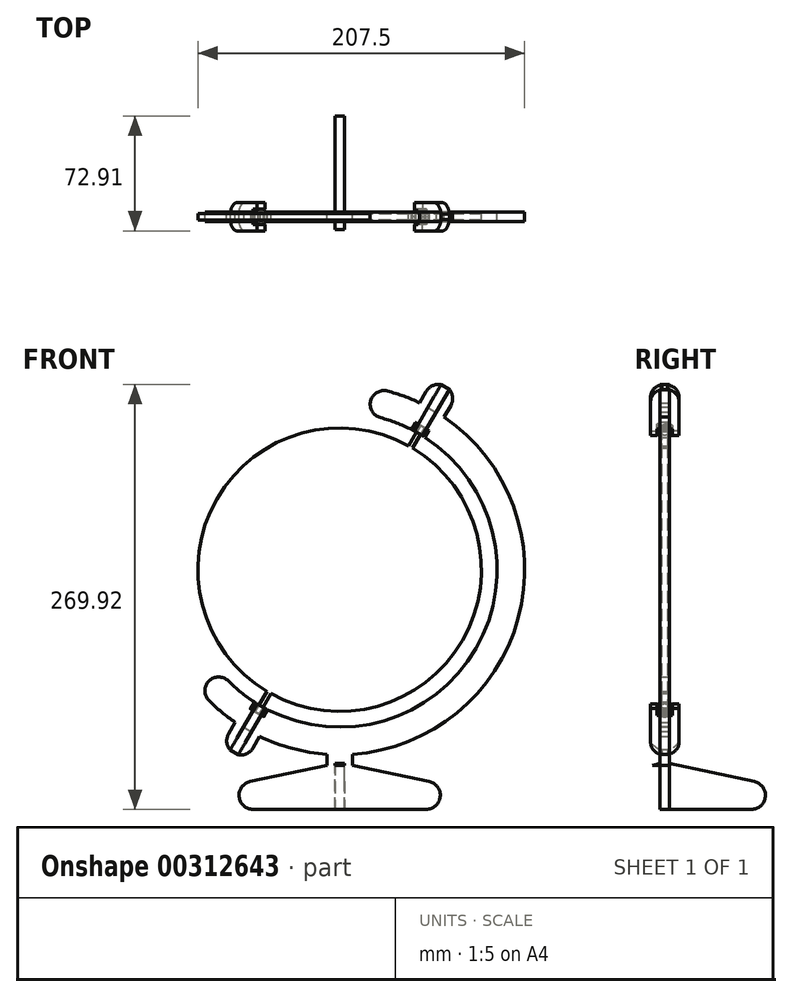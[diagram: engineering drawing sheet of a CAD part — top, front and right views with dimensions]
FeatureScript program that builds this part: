
annotation { "Feature Type Name" : "Feature", "Feature Type Description" : "" }
export const myFeature = defineFeature(function(context is Context, id is Id, definition is map)
    precondition{}
    {
        {
            var Q0;
            Q0=qCreatedBy(makeId("Front.planeOp"),FACE);
            var sketch = newSketch(context, id + "F0", { "sketchPlane" : qUnion([Q0])});
            skLineSegment(sketch, "E0", {"start": v(-16.98, 17.96) * mm, "end": v(-16.98, 0) * mm, "construction": true});
            skLineSegment(sketch, "E1", {"start": v(-16.98, 0) * mm, "end": v(0, 0) * mm, "construction": true});
            skLineSegment(sketch, "E2", {"start": v(-16.98, 17.96) * mm, "end": v(-16.98, 117.96) * mm, "construction": true});
            skLineSegment(sketch, "E3", {"start": v(-16.98, 17.96) * mm, "end": v(8.9, 114.55) * mm, "construction": true});
            skLineSegment(sketch, "E4", {"start": v(8.9, 114.55) * mm, "end": v(13.43, 131.46) * mm, "construction": true});
            skLineSegment(sketch, "E5", {"start": v(-16.98, 17.96) * mm, "end": v(-87.7, -52.75) * mm, "construction": true});
            skLineSegment(sketch, "E6", {"start": v(-87.7, -52.75) * mm, "end": v(-100.07, -65.12) * mm, "construction": true});
            skArc(sketch, "E7", {"start": v(8.9, 114.55) * mm, "mid": v(-103.58, 67.96) * mm, "end": v(-87.7, -52.75) * mm, "construction": true});
            skArc(sketch, "E8", {"start": v(-87.7, -52.75) * mm, "mid": v(69.62, -32.04) * mm, "end": v(8.9, 114.55) * mm});
            skArc(sketch, "E9", {"start": v(-100.07, -65.12) * mm, "mid": v(-92.03, -72.45) * mm, "end": v(-83.35, -79) * mm});
            skArc(sketch, "E10", {"start": v(8.9, 114.55) * mm, "mid": v(2.71, 125.27) * mm, "end": v(13.43, 131.46) * mm});
            skArc(sketch, "E11", {"start": v(-100.07, -65.12) * mm, "mid": v(-100.07, -52.75) * mm, "end": v(-87.7, -52.75) * mm});
            skLineSegment(sketch, "E12", {"start": v(-16.98, 17.96) * mm, "end": v(33.02, 104.56) * mm, "construction": true});
            skLineSegment(sketch, "E13", {"start": v(-16.98, 17.96) * mm, "end": v(-66.98, -68.64) * mm, "construction": true});
            skLineSegment(sketch, "E14", {"start": v(-66.98, -68.64) * mm, "end": v(-75.73, -83.8) * mm, "construction": true});
            skLineSegment(sketch, "E15", {"start": v(33.02, 104.56) * mm, "end": v(41.77, 119.72) * mm, "construction": true});
            skLineSegment(sketch, "E16", {"start": v(33.8, 123.92) * mm, "end": v(37.97, 131.15) * mm});
            skLineSegment(sketch, "E17", {"start": v(49.39, 114.92) * mm, "end": v(53.56, 122.15) * mm});
            skLineSegment(sketch, "E18", {"start": v(41.77, 119.72) * mm, "end": v(45.77, 126.65) * mm, "construction": true});
            skLineSegment(sketch, "E19", {"start": v(45.77, 126.65) * mm, "end": v(53.56, 122.15) * mm, "construction": true});
            skLineSegment(sketch, "E20", {"start": v(45.77, 126.65) * mm, "end": v(37.97, 131.15) * mm, "construction": true});
            skArc(sketch, "E21", {"start": v(37.97, 131.15) * mm, "mid": v(50.27, 134.44) * mm, "end": v(53.56, 122.15) * mm});
            skLineSegment(sketch, "E22", {"start": v(-75.73, -83.8) * mm, "end": v(-79.73, -90.72) * mm, "construction": true});
            skLineSegment(sketch, "E23", {"start": v(-67.77, -88) * mm, "end": v(-71.94, -95.22) * mm});
            skLineSegment(sketch, "E24", {"start": v(-71.94, -95.22) * mm, "end": v(-79.73, -90.72) * mm, "construction": true});
            skLineSegment(sketch, "E25", {"start": v(-79.73, -90.72) * mm, "end": v(-87.53, -86.22) * mm, "construction": true});
            skLineSegment(sketch, "E26", {"start": v(-87.53, -86.22) * mm, "end": v(-83.35, -79) * mm});
            skArc(sketch, "E27", {"start": v(-87.53, -86.22) * mm, "mid": v(-84.23, -98.52) * mm, "end": v(-71.94, -95.22) * mm});
            skArc(sketch, "E28", {"start": v(-83.35, -79) * mm, "mid": v(-75.73, -83.8) * mm, "end": v(-67.77, -88) * mm, "construction": true});
            skArc(sketch, "E29", {"start": v(-67.77, -88) * mm, "mid": v(-46.9, -95.66) * mm, "end": v(-24.98, -99.27) * mm});
            skArc(sketch, "E30", {"start": v(33.8, 123.92) * mm, "mid": v(23.79, 128.16) * mm, "end": v(13.43, 131.46) * mm});
            skArc(sketch, "E31", {"start": v(49.39, 114.92) * mm, "mid": v(41.77, 119.72) * mm, "end": v(33.8, 123.92) * mm, "construction": true});
            skLineSegment(sketch, "E32", {"start": v(-24.98, -99.27) * mm, "end": v(-24.98, -106.27) * mm});
            skLineSegment(sketch, "E33", {"start": v(-16.98, 17.96) * mm, "end": v(-16.98, -82.04) * mm, "construction": true});
            skLineSegment(sketch, "E34", {"start": v(-16.98, -82.04) * mm, "end": v(-16.98, -99.54) * mm, "construction": true});
            skLineSegment(sketch, "E35", {"start": v(-24.98, -106.27) * mm, "end": v(-16.98, -99.54) * mm, "construction": true});
            skLineSegment(sketch, "E36", {"start": v(-16.98, -134.27) * mm, "end": v(-16.98, -99.54) * mm, "construction": true});
            skLineSegment(sketch, "E37", {"start": v(-24.98, -106.27) * mm, "end": v(-71.98, -116.26) * mm});
            skLineSegment(sketch, "E38", {"start": v(-16.98, -134.27) * mm, "end": v(-71.98, -134.27) * mm});
            skLineSegment(sketch, "E39", {"start": v(-71.98, -134.27) * mm, "end": v(-71.98, -116.26) * mm, "construction": true});
            skLineSegment(sketch, "E40", {"start": v(-71.98, -116.26) * mm, "end": v(-73.83, -116.65) * mm});
            skArc(sketch, "E41", {"start": v(-73.83, -116.65) * mm, "mid": v(-80.84, -126.3) * mm, "end": v(-71.98, -134.27) * mm});
            skArc(sketch, "E42", {"start": v(-71.98, -134.27) * mm, "mid": v(-63.13, -124.43) * mm, "end": v(-73.83, -116.65) * mm, "construction": true});
            skLineSegment(sketch, "E43.MirrorCS", {"start": v(-8.98, -99.27) * mm, "end": v(-8.98, -106.27) * mm});
            skLineSegment(sketch, "E44.MirrorCS", {"start": v(-8.98, -106.27) * mm, "end": v(38.02, -116.26) * mm});
            skLineSegment(sketch, "E45.MirrorCS", {"start": v(38.02, -116.26) * mm, "end": v(39.87, -116.65) * mm});
            skArc(sketch, "E46.MirrorCS", {"start": v(39.87, -116.65) * mm, "mid": v(46.87, -126.3) * mm, "end": v(38.02, -134.27) * mm});
            skLineSegment(sketch, "E47.MirrorCS", {"start": v(-16.98, -134.27) * mm, "end": v(38.02, -134.27) * mm});
            skArc(sketch, "E48", {"start": v(-24.98, -99.27) * mm, "mid": v(-16.98, -99.54) * mm, "end": v(-8.98, -99.27) * mm, "construction": true});
            skArc(sketch, "E49", {"start": v(-8.98, -99.27) * mm, "mid": v(96.38, -12.93) * mm, "end": v(49.39, 114.92) * mm});
            skSolve(sketch);
        }
        {
            var Q0;
            Q0=makeQuery(id+"F0.imprint","IMPRINT",FACE,{"disambiguationData":[TD([[makeQuery(id+"F0.imprint","IMPRINT",EDGE,{"derivedFrom":sQuery(id+"F0.wireOp",EDGE,"E8")}),-1.0]])]});
            extrude(context, id + "F1", {"entities" : qUnion([Q0]), "depth" : 3 * mm, "hasSecondDirection" : true, "secondDirectionOppositeDirection" : true, "secondDirectionDepth" : 3 * mm});
        }
        {
            var Q0;
            Q0=makeQuery(id+"F1.opExtrude","CAP_FACE",FACE,{"disambiguationData":[OSD([sQuery(id+"F0.wireOp",EDGE,"E8"),sQuery(id+"F0.wireOp",EDGE,"E9"),sQuery(id+"F0.wireOp",EDGE,"E10"),sQuery(id+"F0.wireOp",EDGE,"E11"),sQuery(id+"F0.wireOp",EDGE,"E16"),sQuery(id+"F0.wireOp",EDGE,"E17"),sQuery(id+"F0.wireOp",EDGE,"E21"),sQuery(id+"F0.wireOp",EDGE,"E23"),sQuery(id+"F0.wireOp",EDGE,"E26"),sQuery(id+"F0.wireOp",EDGE,"E27"),sQuery(id+"F0.wireOp",EDGE,"E29"),sQuery(id+"F0.wireOp",EDGE,"E30"),sQuery(id+"F0.wireOp",EDGE,"E32"),sQuery(id+"F0.wireOp",EDGE,"E37"),sQuery(id+"F0.wireOp",EDGE,"E38"),sQuery(id+"F0.wireOp",EDGE,"E40"),sQuery(id+"F0.wireOp",EDGE,"E41"),sQuery(id+"F0.wireOp",EDGE,"E43.MirrorCS"),sQuery(id+"F0.wireOp",EDGE,"E44.MirrorCS"),sQuery(id+"F0.wireOp",EDGE,"E45.MirrorCS"),sQuery(id+"F0.wireOp",EDGE,"E46.MirrorCS"),sQuery(id+"F0.wireOp",EDGE,"E47.MirrorCS"),sQuery(id+"F0.wireOp",EDGE,"E49")])],"isStart":false});
            var sketch = newSketch(context, id + "F2", { "sketchPlane" : qUnion([Q0])});
            skLineSegment(sketch, "E50", {"start": v(-24.98, -106.27) * mm, "end": v(-8.98, -106.27) * mm, "construction": true});
            skLineSegment(sketch, "E51", {"start": v(-16.98, -106.27) * mm, "end": v(-16.98, -120.27) * mm, "construction": true});
            skLineSegment(sketch, "E52", {"start": v(-16.98, -120.27) * mm, "end": v(-16.98, -134.27) * mm, "construction": true});
            skLineSegment(sketch, "E53", {"start": v(-16.98, -120.27) * mm, "end": v(-13.98, -120.27) * mm});
            skLineSegment(sketch, "E54", {"start": v(-13.98, -120.27) * mm, "end": v(-13.98, -134.27) * mm});
            skLineSegment(sketch, "E55", {"start": v(-16.98, -120.27) * mm, "end": v(-19.98, -120.27) * mm});
            skLineSegment(sketch, "E56", {"start": v(-19.98, -120.27) * mm, "end": v(-19.98, -134.27) * mm});
            skLineSegment(sketch, "E57", {"start": v(-19.98, -134.27) * mm, "end": v(-16.98, -134.27) * mm});
            skLineSegment(sketch, "E58", {"start": v(-13.98, -134.27) * mm, "end": v(-16.98, -134.27) * mm});
            skSolve(sketch);
        }
        {
            var Q0;
            Q0=makeQuery(id+"F2.imprint","IMPRINT",FACE,{"disambiguationData":[TD([[makeQuery(id+"F2.imprint","IMPRINT",EDGE,{"derivedFrom":sQuery(id+"F2.wireOp",EDGE,"E53")}),-1.0]])]});
            var Q1;
            Q1=makeQuery(id+"F1.opExtrude","CAP_FACE",FACE,{"disambiguationData":[OSD([sQuery(id+"F0.wireOp",EDGE,"E8"),sQuery(id+"F0.wireOp",EDGE,"E9"),sQuery(id+"F0.wireOp",EDGE,"E10"),sQuery(id+"F0.wireOp",EDGE,"E11"),sQuery(id+"F0.wireOp",EDGE,"E16"),sQuery(id+"F0.wireOp",EDGE,"E17"),sQuery(id+"F0.wireOp",EDGE,"E21"),sQuery(id+"F0.wireOp",EDGE,"E23"),sQuery(id+"F0.wireOp",EDGE,"E26"),sQuery(id+"F0.wireOp",EDGE,"E27"),sQuery(id+"F0.wireOp",EDGE,"E29"),sQuery(id+"F0.wireOp",EDGE,"E30"),sQuery(id+"F0.wireOp",EDGE,"E32"),sQuery(id+"F0.wireOp",EDGE,"E37"),sQuery(id+"F0.wireOp",EDGE,"E38"),sQuery(id+"F0.wireOp",EDGE,"E40"),sQuery(id+"F0.wireOp",EDGE,"E41"),sQuery(id+"F0.wireOp",EDGE,"E43.MirrorCS"),sQuery(id+"F0.wireOp",EDGE,"E44.MirrorCS"),sQuery(id+"F0.wireOp",EDGE,"E45.MirrorCS"),sQuery(id+"F0.wireOp",EDGE,"E46.MirrorCS"),sQuery(id+"F0.wireOp",EDGE,"E47.MirrorCS"),sQuery(id+"F0.wireOp",EDGE,"E49")])],"isStart":true});
            extrude(context, id + "F3", {"entities" : qUnion([Q0]), "operationType" : NewBodyOperationType.REMOVE, "endBound" : BoundingType.UP_TO_SURFACE, "oppositeDirection" : true, "endBoundEntityFace" : qUnion([Q1]), "depth" : 25 * mm});
        }
        {
            var Q0;
            Q0=makeQuery(id+"F3.boolean.opBoolean","COPY",FACE,{"derivedFrom":makeQuery(id+"F3.opExtrude","SWEPT_FACE",FACE,{"disambiguationData":[OSD([sQuery(id+"F2.wireOp",EDGE,"E53"),sQuery(id+"F2.wireOp",EDGE,"E55")])]})});
            var Q1;
            {var subQ1=sQuery(id+"F0.wireOp",EDGE,"E47.MirrorCS");var subQ6=sQuery(id+"F0.wireOp",EDGE,"E41");var subQ8=sQuery(id+"F0.wireOp",EDGE,"E38");Q1=makeQuery(id+"F3.boolean.opBoolean","SPLIT",FACE,{"disambiguationData":[TD([makeQuery(id+"F1.opExtrude","SWEPT_FACE",FACE,{"disambiguationData":[OSD([subQ6])]})])],"derivedFrom":makeQuery(id+"F1.opExtrude","SWEPT_FACE",FACE,{"disambiguationData":[OSD([subQ8,subQ1])]})});}
            extrude(context, id + "F4", {"entities" : qUnion([Q0]), "endBound" : BoundingType.UP_TO_SURFACE, "endBoundEntityFace" : qUnion([Q1]), "depth" : 25 * mm});
        }
        {
            var Q0;
            Q0=makeQuery(id+"F4.opExtrude","SWEPT_FACE",FACE,{"disambiguationData":[OSD([sQuery(id+"F2.wireOp",EDGE,"E55"),sQuery(id+"F2.wireOp",EDGE,"E56")])]});
            var sketch = newSketch(context, id + "F5", { "sketchPlane" : qUnion([Q0])});
            skLineSegment(sketch, "E59", {"start": v(0, -134.27) * mm, "end": v(-55, -134.27) * mm});
            skLineSegment(sketch, "E60", {"start": v(0, -134.27) * mm, "end": v(0, -120.27) * mm, "construction": true});
            skLineSegment(sketch, "E61", {"start": v(0, -120.27) * mm, "end": v(0, -106.27) * mm, "construction": true});
            skLineSegment(sketch, "E62", {"start": v(0, -106.27) * mm, "end": v(-8, -106.27) * mm});
            skLineSegment(sketch, "E63", {"start": v(-8, -106.27) * mm, "end": v(-55, -116.26) * mm});
            skLineSegment(sketch, "E64", {"start": v(-55, -116.26) * mm, "end": v(-55, -134.27) * mm, "construction": true});
            skLineSegment(sketch, "E65", {"start": v(-55, -116.26) * mm, "end": v(-56.85, -116.65) * mm});
            skArc(sketch, "E66", {"start": v(-56.85, -116.65) * mm, "mid": v(-63.86, -126.3) * mm, "end": v(-55, -134.27) * mm});
            skArc(sketch, "E67", {"start": v(-55, -134.27) * mm, "mid": v(-46.14, -124.43) * mm, "end": v(-56.85, -116.65) * mm, "construction": true});
            skLineSegment(sketch, "E68.MirrorCS", {"start": v(0, -134.27) * mm, "end": v(55, -134.27) * mm});
            skArc(sketch, "E69.MirrorCS", {"start": v(56.85, -116.65) * mm, "mid": v(63.86, -126.3) * mm, "end": v(55, -134.27) * mm});
            skLineSegment(sketch, "E70.MirrorCS", {"start": v(55, -116.26) * mm, "end": v(56.85, -116.65) * mm});
            skLineSegment(sketch, "E71.MirrorCS", {"start": v(8, -106.27) * mm, "end": v(55, -116.26) * mm});
            skLineSegment(sketch, "E72.MirrorCS", {"start": v(0, -106.27) * mm, "end": v(8, -106.27) * mm});
            skLineSegment(sketch, "E73", {"start": v(-3, -120.27) * mm, "end": v(-3, -106.27) * mm});
            skLineSegment(sketch, "E74", {"start": v(3, -120.27) * mm, "end": v(3, -106.27) * mm});
            skLineSegment(sketch, "E75", {"start": v(-8, -106.27) * mm, "end": v(0, -104.56) * mm});
            skLineSegment(sketch, "E76", {"start": v(0, -104.56) * mm, "end": v(-3, -106.27) * mm});
            skLineSegment(sketch, "E77.0", {"start": v(3, -99.27) * mm, "end": v(3, -106.27) * mm, "construction": true});
            skLineSegment(sketch, "E78", {"start": v(8, -106.27) * mm, "end": v(3, -105.2) * mm});
            skLineSegment(sketch, "E79", {"start": v(3, -105.2) * mm, "end": v(3, -106.27) * mm});
            skSolve(sketch);
        }
        {
            var Q0;
            {var subQ1=sQuery(id+"F5.wireOp",EDGE,"E69.MirrorCS");Q0=makeQuery(id+"F5.imprint","IMPRINT",FACE,{"disambiguationData":[TD([[makeQuery(id+"F5.imprint","IMPRINT",EDGE,{"derivedFrom":subQ1}),-1.0]])]});}
            var Q1;
            {var subQ0=sQuery(id+"F5.wireOp",EDGE,"E63");Q1=makeQuery(id+"F5.imprint","IMPRINT",FACE,{"disambiguationData":[TD([[makeQuery(id+"F5.imprint","IMPRINT",EDGE,{"derivedFrom":subQ0}),1.0]])]});}
            var Q2;
            {var subQ0=sQuery(id+"F5.wireOp",EDGE,"E75");Q2=makeQuery(id+"F5.imprint","IMPRINT",FACE,{"disambiguationData":[TD([[makeQuery(id+"F5.imprint","IMPRINT",EDGE,{"derivedFrom":subQ0}),-1.0]])]});}
            var Q3;
            {var subQ0=sQuery(id+"F5.wireOp",EDGE,"E78");Q3=makeQuery(id+"F5.imprint","IMPRINT",FACE,{"disambiguationData":[TD([[makeQuery(id+"F5.imprint","IMPRINT",EDGE,{"derivedFrom":subQ0}),1.0]])]});}
            var Q4;
            Q4=makeQuery(id+"F4.opExtrude","SWEPT_FACE",FACE,{"disambiguationData":[OSD([sQuery(id+"F2.wireOp",EDGE,"E53"),sQuery(id+"F2.wireOp",EDGE,"E54")])]});
            extrude(context, id + "F6", {"entities" : qUnion([Q0, Q1, Q2, Q3]), "operationType" : NewBodyOperationType.ADD, "endBound" : BoundingType.UP_TO_SURFACE, "oppositeDirection" : true, "endBoundEntityFace" : qUnion([Q4]), "depth" : 25 * mm});
        }
        {
            var Q0;
            Q0=makeQuery(id+"F1.opExtrude","CAP_FACE",FACE,{"disambiguationData":[OSD([sQuery(id+"F0.wireOp",EDGE,"E8"),sQuery(id+"F0.wireOp",EDGE,"E9"),sQuery(id+"F0.wireOp",EDGE,"E10"),sQuery(id+"F0.wireOp",EDGE,"E11"),sQuery(id+"F0.wireOp",EDGE,"E16"),sQuery(id+"F0.wireOp",EDGE,"E17"),sQuery(id+"F0.wireOp",EDGE,"E21"),sQuery(id+"F0.wireOp",EDGE,"E23"),sQuery(id+"F0.wireOp",EDGE,"E26"),sQuery(id+"F0.wireOp",EDGE,"E27"),sQuery(id+"F0.wireOp",EDGE,"E29"),sQuery(id+"F0.wireOp",EDGE,"E30"),sQuery(id+"F0.wireOp",EDGE,"E32"),sQuery(id+"F0.wireOp",EDGE,"E37"),sQuery(id+"F0.wireOp",EDGE,"E38"),sQuery(id+"F0.wireOp",EDGE,"E40"),sQuery(id+"F0.wireOp",EDGE,"E41"),sQuery(id+"F0.wireOp",EDGE,"E43.MirrorCS"),sQuery(id+"F0.wireOp",EDGE,"E44.MirrorCS"),sQuery(id+"F0.wireOp",EDGE,"E45.MirrorCS"),sQuery(id+"F0.wireOp",EDGE,"E46.MirrorCS"),sQuery(id+"F0.wireOp",EDGE,"E47.MirrorCS"),sQuery(id+"F0.wireOp",EDGE,"E49")])],"isStart":false});
            var sketch = newSketch(context, id + "F7", { "sketchPlane" : qUnion([Q0])});
            skPoint(sketch, "E80.0", {"position": v(-83.35, -79) * mm});
            skPoint(sketch, "E80.1", {"position": v(-67.77, -88) * mm});
            skPoint(sketch, "E81.0", {"position": v(33.8, 123.92) * mm});
            skPoint(sketch, "E81.1", {"position": v(49.39, 114.92) * mm});
            skLineSegment(sketch, "E82", {"start": v(33.8, 123.92) * mm, "end": v(39, 120.92) * mm, "construction": true});
            skLineSegment(sketch, "E83", {"start": v(-83.35, -79) * mm, "end": v(-78.16, -82) * mm, "construction": true});
            skPoint(sketch, "E84.0", {"position": v(-84.23, -98.52) * mm});
            skLineSegment(sketch, "E85", {"start": v(-75.56, -83.5) * mm, "end": v(-84.23, -98.52) * mm, "construction": true});
            skPoint(sketch, "E86.0", {"position": v(50.27, 134.44) * mm});
            skLineSegment(sketch, "E87", {"start": v(41.6, 119.42) * mm, "end": v(50.27, 134.44) * mm, "construction": true});
            skArc(sketch, "E88.0", {"start": v(37.97, 131.15) * mm, "mid": v(42, 134.82) * mm, "end": v(47.41, 135.5) * mm, "construction": true});
            skLineSegment(sketch, "E89", {"start": v(39, 120.92) * mm, "end": v(47.41, 135.5) * mm});
            skLineSegment(sketch, "E90", {"start": v(44.2, 117.92) * mm, "end": v(52.6, 132.5) * mm});
            skLineSegment(sketch, "E91", {"start": v(39, 120.92) * mm, "end": v(41.6, 119.42) * mm});
            skLineSegment(sketch, "E92", {"start": v(41.6, 119.42) * mm, "end": v(44.2, 117.92) * mm});
            skLineSegment(sketch, "E93", {"start": v(44.2, 117.92) * mm, "end": v(49.39, 114.92) * mm, "construction": true});
            skArc(sketch, "E94", {"start": v(47.41, 135.5) * mm, "mid": v(50.27, 134.44) * mm, "end": v(52.6, 132.5) * mm});
            skArc(sketch, "E95", {"start": v(52.6, 132.5) * mm, "mid": v(54.73, 127.47) * mm, "end": v(53.56, 122.15) * mm, "construction": true});
            skArc(sketch, "E96.0", {"start": v(-87.53, -86.22) * mm, "mid": v(-88.7, -91.55) * mm, "end": v(-86.57, -96.57) * mm, "construction": true});
            skLineSegment(sketch, "E97", {"start": v(-72.96, -85) * mm, "end": v(-81.38, -99.57) * mm});
            skLineSegment(sketch, "E98", {"start": v(-78.16, -82) * mm, "end": v(-86.57, -96.57) * mm});
            skLineSegment(sketch, "E99", {"start": v(-78.16, -82) * mm, "end": v(-75.56, -83.5) * mm});
            skLineSegment(sketch, "E100", {"start": v(-75.56, -83.5) * mm, "end": v(-72.96, -85) * mm});
            skLineSegment(sketch, "E101", {"start": v(-72.96, -85) * mm, "end": v(-67.77, -88) * mm, "construction": true});
            skArc(sketch, "E102", {"start": v(-81.38, -99.57) * mm, "mid": v(-75.97, -98.9) * mm, "end": v(-71.94, -95.22) * mm, "construction": true});
            skArc(sketch, "E103", {"start": v(-86.57, -96.57) * mm, "mid": v(-84.23, -98.52) * mm, "end": v(-81.38, -99.57) * mm});
            skSolve(sketch);
        }
        {
            var Q0;
            Q0=makeQuery(id+"F7.imprint","IMPRINT",FACE,{"disambiguationData":[TD([[makeQuery(id+"F7.imprint","IMPRINT",EDGE,{"derivedFrom":sQuery(id+"F7.wireOp",EDGE,"E97")}),-1.0]])]});
            var Q1;
            Q1=makeQuery(id+"F7.imprint","IMPRINT",FACE,{"disambiguationData":[TD([[makeQuery(id+"F7.imprint","IMPRINT",EDGE,{"derivedFrom":sQuery(id+"F7.wireOp",EDGE,"E89")}),-1.0]])]});
            var Q2;
            Q2=makeQuery(id+"F1.opExtrude","CAP_FACE",FACE,{"disambiguationData":[OSD([sQuery(id+"F0.wireOp",EDGE,"E8"),sQuery(id+"F0.wireOp",EDGE,"E9"),sQuery(id+"F0.wireOp",EDGE,"E10"),sQuery(id+"F0.wireOp",EDGE,"E11"),sQuery(id+"F0.wireOp",EDGE,"E16"),sQuery(id+"F0.wireOp",EDGE,"E17"),sQuery(id+"F0.wireOp",EDGE,"E21"),sQuery(id+"F0.wireOp",EDGE,"E23"),sQuery(id+"F0.wireOp",EDGE,"E26"),sQuery(id+"F0.wireOp",EDGE,"E27"),sQuery(id+"F0.wireOp",EDGE,"E29"),sQuery(id+"F0.wireOp",EDGE,"E30"),sQuery(id+"F0.wireOp",EDGE,"E32"),sQuery(id+"F0.wireOp",EDGE,"E37"),sQuery(id+"F0.wireOp",EDGE,"E38"),sQuery(id+"F0.wireOp",EDGE,"E40"),sQuery(id+"F0.wireOp",EDGE,"E41"),sQuery(id+"F0.wireOp",EDGE,"E43.MirrorCS"),sQuery(id+"F0.wireOp",EDGE,"E44.MirrorCS"),sQuery(id+"F0.wireOp",EDGE,"E45.MirrorCS"),sQuery(id+"F0.wireOp",EDGE,"E46.MirrorCS"),sQuery(id+"F0.wireOp",EDGE,"E47.MirrorCS"),sQuery(id+"F0.wireOp",EDGE,"E49")])],"isStart":true});
            extrude(context, id + "F8", {"entities" : qUnion([Q0, Q1]), "operationType" : NewBodyOperationType.REMOVE, "endBound" : BoundingType.UP_TO_SURFACE, "oppositeDirection" : true, "endBoundEntityFace" : qUnion([Q2]), "depth" : 25 * mm});
        }
        {
            var Q0;
            Q0=makeQuery(id+"F8.boolean.opBoolean","COPY",FACE,{"derivedFrom":makeQuery(id+"F8.opExtrude","SWEPT_FACE",FACE,{"disambiguationData":[OSD([sQuery(id+"F7.wireOp",EDGE,"E97")])]})});
            var sketch = newSketch(context, id + "F9", { "sketchPlane" : qUnion([Q0])});
            skLineSegment(sketch, "E104.0", {"start": v(3, 107.06) * mm, "end": v(3, -92.94) * mm, "construction": true});
            skPoint(sketch, "E105.0", {"position": v(0, 141.05) * mm});
            skLineSegment(sketch, "E106.0", {"start": v(-3, -110.1) * mm, "end": v(3, -110.1) * mm});
            skLineSegment(sketch, "E107", {"start": v(0, -110.1) * mm, "end": v(0, -118.1) * mm, "construction": true});
            skLineSegment(sketch, "E108", {"start": v(0, -118.1) * mm, "end": v(0, -127.1) * mm, "construction": true});
            skPoint(sketch, "E108.endSnap0", {"position": v(0, -126.92) * mm});
            skArc(sketch, "E109", {"start": v(0, -127.1) * mm, "mid": v(-0.87, -127.05) * mm, "end": v(-1.74, -126.92) * mm, "construction": true});
            skArc(sketch, "E110", {"start": v(0, -127.1) * mm, "mid": v(0.87, -127.05) * mm, "end": v(1.74, -126.92) * mm, "construction": true});
            skLineSegment(sketch, "E111.0", {"start": v(-3, -126.92) * mm, "end": v(-1.74, -126.92) * mm, "construction": true});
            skLineSegment(sketch, "E112", {"start": v(-1.74, -126.92) * mm, "end": v(1.74, -126.92) * mm});
            skLineSegment(sketch, "E113", {"start": v(1.74, -126.92) * mm, "end": v(3, -126.92) * mm, "construction": true});
            skArc(sketch, "E114", {"start": v(-1.74, -126.92) * mm, "mid": v(-6.95, -123.8) * mm, "end": v(-9, -118.1) * mm});
            skArc(sketch, "E115", {"start": v(1.74, -126.92) * mm, "mid": v(6.95, -123.8) * mm, "end": v(9, -118.1) * mm});
            skLineSegment(sketch, "E116", {"start": v(-3, -110.1) * mm, "end": v(-3, -92.94) * mm});
            skLineSegment(sketch, "E117", {"start": v(-3, -92.94) * mm, "end": v(3, -92.94) * mm});
            skLineSegment(sketch, "E118", {"start": v(3, -110.1) * mm, "end": v(3, -92.94) * mm});
            skLineSegment(sketch, "E119", {"start": v(-9, -118.1) * mm, "end": v(-9, -92.94) * mm});
            skLineSegment(sketch, "E120", {"start": v(-9, -92.94) * mm, "end": v(-3, -92.94) * mm});
            skLineSegment(sketch, "E121", {"start": v(3, -92.94) * mm, "end": v(9, -92.94) * mm});
            skLineSegment(sketch, "E122", {"start": v(9, -92.94) * mm, "end": v(9, -118.1) * mm});
            skLineSegment(sketch, "E123.0", {"start": v(-3, 124.22) * mm, "end": v(3, 124.22) * mm});
            skLineSegment(sketch, "E124", {"start": v(0, 124.22) * mm, "end": v(0, 132.22) * mm, "construction": true});
            skLineSegment(sketch, "E125", {"start": v(0, 132.22) * mm, "end": v(0, 141.22) * mm, "construction": true});
            skArc(sketch, "E126", {"start": v(0, 141.22) * mm, "mid": v(0.87, 141.18) * mm, "end": v(1.74, 141.05) * mm, "construction": true});
            skArc(sketch, "E127", {"start": v(0, 141.22) * mm, "mid": v(-0.87, 141.18) * mm, "end": v(-1.74, 141.05) * mm, "construction": true});
            skLineSegment(sketch, "E128", {"start": v(0, 141.05) * mm, "end": v(1.74, 141.05) * mm});
            skLineSegment(sketch, "E129", {"start": v(0, 141.05) * mm, "end": v(-1.74, 141.05) * mm});
            skArc(sketch, "E130", {"start": v(-1.74, 141.05) * mm, "mid": v(-6.95, 137.94) * mm, "end": v(-9, 132.22) * mm});
            skArc(sketch, "E131", {"start": v(1.74, 141.05) * mm, "mid": v(6.95, 137.94) * mm, "end": v(9, 132.22) * mm});
            skLineSegment(sketch, "E132", {"start": v(3, 107.06) * mm, "end": v(3, 124.22) * mm});
            skLineSegment(sketch, "E133", {"start": v(3, 107.06) * mm, "end": v(-3, 107.06) * mm, "construction": true});
            skLineSegment(sketch, "E134", {"start": v(-3, 107.06) * mm, "end": v(-3, 124.22) * mm});
            skLineSegment(sketch, "E135", {"start": v(9, 132.22) * mm, "end": v(9, 107.06) * mm});
            skLineSegment(sketch, "E136", {"start": v(-9, 132.22) * mm, "end": v(-9, 107.06) * mm});
            skLineSegment(sketch, "E137", {"start": v(-9, 107.06) * mm, "end": v(-3, 107.06) * mm});
            skLineSegment(sketch, "E138", {"start": v(9, 107.06) * mm, "end": v(3, 107.06) * mm});
            skSolve(sketch);
        }
        {
            var Q0;
            {var subQ1=sQuery(id+"F9.wireOp",EDGE,"E118");Q0=makeQuery(id+"F9.imprint","IMPRINT",FACE,{"disambiguationData":[TD([[makeQuery(id+"F9.imprint","IMPRINT",EDGE,{"derivedFrom":subQ1}),-1.0]])]});}
            var Q1;
            {var subQ3=sQuery(id+"F9.wireOp",EDGE,"E112");Q1=makeQuery(id+"F9.imprint","IMPRINT",FACE,{"disambiguationData":[TD([[makeQuery(id+"F9.imprint","IMPRINT",EDGE,{"derivedFrom":subQ3}),1.0]])]});}
            var Q2;
            {var subQ1=sQuery(id+"F9.wireOp",EDGE,"E116");Q2=makeQuery(id+"F9.imprint","IMPRINT",FACE,{"disambiguationData":[TD([[makeQuery(id+"F9.imprint","IMPRINT",EDGE,{"derivedFrom":subQ1}),1.0]])]});}
            var Q3;
            Q3=makeQuery(id+"F9.imprint","IMPRINT",FACE,{"disambiguationData":[TD([[makeQuery(id+"F9.imprint","IMPRINT",EDGE,{"derivedFrom":sQuery(id+"F9.wireOp",EDGE,"E123.0")}),1.0]])]});
            var Q4;
            Q4=makeQuery(id+"F8.boolean.opBoolean","COPY",FACE,{"derivedFrom":makeQuery(id+"F8.opExtrude","SWEPT_FACE",FACE,{"disambiguationData":[OSD([sQuery(id+"F7.wireOp",EDGE,"E98")])]})});
            extrude(context, id + "F10", {"entities" : qUnion([Q0, Q1, Q2, Q3]), "endBound" : BoundingType.UP_TO_SURFACE, "endBoundEntityFace" : qUnion([Q4]), "depth" : 25 * mm});
        }
        {
            var Q0;
            Q0=makeQuery(id+"F10.opExtrude","SWEPT_FACE",FACE,{"disambiguationData":[OSD([sQuery(id+"F9.wireOp",EDGE,"E120")])]});
            var sketch = newSketch(context, id + "F11", { "sketchPlane" : qUnion([Q0])});
            skLineSegment(sketch, "E139.0", {"start": v(-20.69, 3) * mm, "end": v(-20.69, -3) * mm, "construction": true});
            skLineSegment(sketch, "E139.1", {"start": v(-26.69, -3) * mm, "end": v(-20.69, -3) * mm, "construction": true});
            skLineSegment(sketch, "E139.2", {"start": v(-26.69, 3) * mm, "end": v(-26.69, -3) * mm, "construction": true});
            skLineSegment(sketch, "E139.3", {"start": v(-26.69, 3) * mm, "end": v(-20.69, 3) * mm, "construction": true});
            skLineSegment(sketch, "E140", {"start": v(-20.69, 3) * mm, "end": v(-26.69, -3) * mm, "construction": true});
            skCircle(sketch, "E141", {"center": v(-23.69, 0) * mm, "radius": 4.9 * mm});
            skLineSegment(sketch, "E142.0", {"start": v(-20.69, 4.9) * mm, "end": v(-20.69, 3) * mm});
            skLineSegment(sketch, "E142.1", {"start": v(-26.69, 4.9) * mm, "end": v(-26.69, 3) * mm});
            skLineSegment(sketch, "E142.2", {"start": v(-26.69, -3) * mm, "end": v(-26.69, -4.9) * mm});
            skLineSegment(sketch, "E142.3", {"start": v(-20.69, -3) * mm, "end": v(-20.69, -4.9) * mm});
            skLineSegment(sketch, "E143", {"start": v(-26.69, 4.9) * mm, "end": v(-20.69, 4.9) * mm});
            skLineSegment(sketch, "E144", {"start": v(-20.69, -4.9) * mm, "end": v(-26.69, -4.9) * mm});
            skPoint(sketch, "E144.endSnap0", {"position": v(-26.69, -6) * mm});
            skLineSegment(sketch, "E145.0", {"start": v(-28.59, 3) * mm, "end": v(-26.69, 3) * mm});
            skLineSegment(sketch, "E145.1", {"start": v(-28.59, -3) * mm, "end": v(-26.69, -3) * mm});
            skLineSegment(sketch, "E146", {"start": v(-18.79, 3) * mm, "end": v(-18.79, -3) * mm});
            skLineSegment(sketch, "E147", {"start": v(-28.59, 3) * mm, "end": v(-28.59, -3) * mm});
            skPoint(sketch, "E148.orphan", {"position": v(76.31, -3) * mm});
            skPoint(sketch, "E149.orphan", {"position": v(76.31, 3) * mm});
            skPoint(sketch, "E150.orphan", {"position": v(-20.69, 9) * mm});
            skPoint(sketch, "E151.orphan", {"position": v(-26.69, 9) * mm});
            skPoint(sketch, "E152.orphan", {"position": v(-26.69, -9) * mm});
            skPoint(sketch, "E153.orphan", {"position": v(-20.69, -9) * mm});
            skPoint(sketch, "E154.orphan", {"position": v(-49.57, -3) * mm});
            skPoint(sketch, "E155.orphan", {"position": v(-49.57, 3) * mm});
            skLineSegment(sketch, "E156", {"start": v(-20.69, 3) * mm, "end": v(-18.79, 3) * mm});
            skLineSegment(sketch, "E157", {"start": v(-20.69, -3) * mm, "end": v(-18.79, -3) * mm});
            skCircle(sketch, "E158", {"center": v(-23.69, 0) * mm, "radius": 2.5 * mm});
            skSolve(sketch);
        }
        {
            var Q0;
            Q0=makeQuery(id+"F11.imprint","IMPRINT",FACE,{"disambiguationData":[TD([[makeQuery(id+"F11.imprint","IMPRINT",EDGE,{"derivedFrom":sQuery(id+"F11.wireOp",EDGE,"E142.0")}),-1.0]])]});
            var Q1;
            Q1=makeQuery(id+"F11.imprint","IMPRINT",FACE,{"disambiguationData":[TD([[makeQuery(id+"F11.imprint","IMPRINT",EDGE,{"derivedFrom":sQuery(id+"F11.wireOp",EDGE,"E142.2")}),1.0]])]});
            var Q2;
            {var subQ1=makeQuery(id+"F10.opExtrude","SWEPT_EDGE",EDGE,{"disambiguationData":[OSD([sQuery(id+"F9.wireOp",EDGE,"E116"),sQuery(id+"F9.wireOp",EDGE,"E117"),sQuery(id+"F9.wireOp",EDGE,"E120")])]});Q2=makeQuery(id+"F11.imprint","IMPRINT",FACE,{"disambiguationData":[TD([[makeQuery(id+"F11.imprint","IMPRINT",EDGE,{"derivedFrom":subQ1}),1.0]])]});}
            var Q3;
            {var subQ0=sQuery(id+"F11.wireOp",EDGE,"E142.1");var subQ1=sQuery(id+"F11.wireOp",EDGE,"E141");var subQ2=makeQuery(id+"F11.imprint","INTERSECT",VERTEX,{"derivedFrom":[subQ1,subQ0]});Q3=makeQuery(id+"F11.imprint","IMPRINT",FACE,{"disambiguationData":[TD([[makeQuery(id+"F11.imprint","IMPRINT",EDGE,{"disambiguationData":[TD([[subQ2,1.0]])],"derivedFrom":subQ1}),-1.0]])]});}
            var Q4;
            Q4=makeQuery(id+"F11.imprint","IMPRINT",FACE,{"disambiguationData":[TD([[makeQuery(id+"F11.imprint","IMPRINT",EDGE,{"derivedFrom":sQuery(id+"F11.wireOp",EDGE,"E158")}),1.0]])]});
            var Q5;
            {var subQ0=sQuery(id+"F11.wireOp",EDGE,"E156");var subQ1=sQuery(id+"F11.wireOp",EDGE,"E141");var subQ2=makeQuery(id+"F11.imprint","INTERSECT",VERTEX,{"derivedFrom":[subQ1,subQ0]});Q5=makeQuery(id+"F11.imprint","IMPRINT",FACE,{"disambiguationData":[TD([[makeQuery(id+"F11.imprint","IMPRINT",EDGE,{"disambiguationData":[TD([[subQ2,-1.0]])],"derivedFrom":subQ1}),1.0]])]});}
            var Q6;
            {var subQ0=sQuery(id+"F11.wireOp",EDGE,"E156");var subQ1=sQuery(id+"F11.wireOp",EDGE,"E141");var subQ2=makeQuery(id+"F11.imprint","INTERSECT",VERTEX,{"derivedFrom":[subQ1,subQ0]});Q6=makeQuery(id+"F11.imprint","IMPRINT",FACE,{"disambiguationData":[TD([[makeQuery(id+"F11.imprint","IMPRINT",EDGE,{"disambiguationData":[TD([[subQ2,1.0]])],"derivedFrom":subQ1}),-1.0]])]});}
            var Q7;
            Q7=makeQuery(id+"F11.imprint","IMPRINT",FACE,{"disambiguationData":[TD([[makeQuery(id+"F11.imprint","IMPRINT",EDGE,{"derivedFrom":sQuery(id+"F11.wireOp",EDGE,"E158")}),-1.0]])]});
            var Q8;
            {var subQ0=sQuery(id+"F11.wireOp",EDGE,"E146");var subQ1=sQuery(id+"F11.wireOp",EDGE,"E141");var subQ2=makeQuery(id+"F11.imprint","INTERSECT",VERTEX,{"derivedFrom":[subQ1,subQ0]});Q8=makeQuery(id+"F11.imprint","IMPRINT",FACE,{"disambiguationData":[TD([[makeQuery(id+"F11.imprint","IMPRINT",EDGE,{"disambiguationData":[TD([[subQ2,1.0]])],"derivedFrom":subQ1}),-1.0]])]});}
            var Q9;
            {var subQ0=sQuery(id+"F11.wireOp",EDGE,"E142.3");var subQ1=sQuery(id+"F11.wireOp",EDGE,"E141");var subQ2=makeQuery(id+"F11.imprint","INTERSECT",VERTEX,{"derivedFrom":[subQ1,subQ0]});Q9=makeQuery(id+"F11.imprint","IMPRINT",FACE,{"disambiguationData":[TD([[makeQuery(id+"F11.imprint","IMPRINT",EDGE,{"disambiguationData":[TD([[subQ2,-1.0]])],"derivedFrom":subQ1}),1.0]])]});}
            var Q10;
            {var subQ0=sQuery(id+"F11.wireOp",EDGE,"E144");var subQ1=sQuery(id+"F11.wireOp",EDGE,"E141");var subQ2=makeQuery(id+"F11.imprint","INTERSECT",VERTEX,{"derivedFrom":[subQ1,subQ0]});Q10=makeQuery(id+"F11.imprint","IMPRINT",FACE,{"disambiguationData":[TD([[makeQuery(id+"F11.imprint","IMPRINT",EDGE,{"disambiguationData":[TD([[subQ2,-1.0]])],"derivedFrom":subQ1}),-1.0]])]});}
            var Q11;
            {var subQ0=sQuery(id+"F11.wireOp",EDGE,"E145.1");var subQ1=sQuery(id+"F11.wireOp",EDGE,"E141");var subQ2=makeQuery(id+"F11.imprint","INTERSECT",VERTEX,{"derivedFrom":[subQ1,subQ0]});Q11=makeQuery(id+"F11.imprint","IMPRINT",FACE,{"disambiguationData":[TD([[makeQuery(id+"F11.imprint","IMPRINT",EDGE,{"disambiguationData":[TD([[subQ2,-1.0]])],"derivedFrom":subQ1}),1.0]])]});}
            var Q12;
            {var subQ0=sQuery(id+"F11.wireOp",EDGE,"E147");var subQ1=sQuery(id+"F11.wireOp",EDGE,"E141");var subQ2=makeQuery(id+"F11.imprint","INTERSECT",VERTEX,{"derivedFrom":[subQ1,subQ0]});Q12=makeQuery(id+"F11.imprint","IMPRINT",FACE,{"disambiguationData":[TD([[makeQuery(id+"F11.imprint","IMPRINT",EDGE,{"disambiguationData":[TD([[subQ2,-1.0]])],"derivedFrom":subQ1}),-1.0]])]});}
            var Q13;
            {var subQ0=sQuery(id+"F11.wireOp",EDGE,"E145.0");var subQ1=sQuery(id+"F11.wireOp",EDGE,"E141");var subQ2=makeQuery(id+"F11.imprint","INTERSECT",VERTEX,{"derivedFrom":[subQ1,subQ0]});Q13=makeQuery(id+"F11.imprint","IMPRINT",FACE,{"disambiguationData":[TD([[makeQuery(id+"F11.imprint","IMPRINT",EDGE,{"disambiguationData":[TD([[subQ2,-1.0]])],"derivedFrom":subQ1}),-1.0]])]});}
            var Q14;
            {var subQ0=sQuery(id+"F11.wireOp",EDGE,"E142.1");var subQ1=sQuery(id+"F11.wireOp",EDGE,"E141");var subQ2=makeQuery(id+"F11.imprint","INTERSECT",VERTEX,{"derivedFrom":[subQ1,subQ0]});Q14=makeQuery(id+"F11.imprint","IMPRINT",FACE,{"disambiguationData":[TD([[makeQuery(id+"F11.imprint","IMPRINT",EDGE,{"disambiguationData":[TD([[subQ2,-1.0]])],"derivedFrom":subQ1}),1.0]])]});}
            extrude(context, id + "F12", {"entities" : qUnion([Q0, Q1, Q2, Q3, Q4, Q5, Q6, Q7, Q8, Q9, Q10, Q11, Q12, Q13, Q14]), "operationType" : NewBodyOperationType.REMOVE, "depth" : 5 * mm, "hasSecondDirection" : true, "secondDirectionOppositeDirection" : true, "secondDirectionDepth" : 5 * mm});
        }
        {
            var Q0;
            Q0=makeQuery(id+"F10.opExtrude","SWEPT_FACE",FACE,{"disambiguationData":[OSD([sQuery(id+"F9.wireOp",EDGE,"E137")])]});
            var sketch = newSketch(context, id + "F13", { "sketchPlane" : qUnion([Q0])});
            skLineSegment(sketch, "E159.0", {"start": v(-20.69, 4.9) * mm, "end": v(-26.69, 4.9) * mm});
            skLineSegment(sketch, "E159.1", {"start": v(-26.69, 3) * mm, "end": v(-26.69, 4.9) * mm});
            skLineSegment(sketch, "E159.2", {"start": v(-28.59, 3) * mm, "end": v(-26.69, 3) * mm});
            skLineSegment(sketch, "E159.3", {"start": v(-28.59, -3) * mm, "end": v(-28.59, 3) * mm});
            skLineSegment(sketch, "E159.4", {"start": v(-28.59, -3) * mm, "end": v(-26.69, -3) * mm});
            skLineSegment(sketch, "E159.5", {"start": v(-26.69, -4.9) * mm, "end": v(-26.69, -3) * mm});
            skLineSegment(sketch, "E159.6", {"start": v(-26.69, -4.9) * mm, "end": v(-20.69, -4.9) * mm});
            skLineSegment(sketch, "E159.7", {"start": v(-20.69, -4.9) * mm, "end": v(-20.69, -3) * mm});
            skLineSegment(sketch, "E159.8", {"start": v(-20.69, -3) * mm, "end": v(-18.79, -3) * mm});
            skLineSegment(sketch, "E159.9", {"start": v(-18.79, -3) * mm, "end": v(-18.79, 3) * mm});
            skLineSegment(sketch, "E159.10", {"start": v(-20.69, 3) * mm, "end": v(-18.79, 3) * mm});
            skLineSegment(sketch, "E159.11", {"start": v(-20.69, 3) * mm, "end": v(-20.69, 4.9) * mm});
            skCircle(sketch, "E160.0", {"center": v(-23.69, 0) * mm, "radius": 4.9 * mm});
            skCircle(sketch, "E160.1", {"center": v(-23.69, 0) * mm, "radius": 2.5 * mm});
            skSolve(sketch);
        }
        {
            var Q0;
            Q0=makeQuery(id+"F13.imprint","IMPRINT",FACE,{"disambiguationData":[TD([[makeQuery(id+"F13.imprint","IMPRINT",EDGE,{"derivedFrom":sQuery(id+"F13.wireOp",EDGE,"E160.1")}),-1.0]])]});
            var Q1;
            Q1=makeQuery(id+"F13.imprint","IMPRINT",FACE,{"disambiguationData":[TD([[makeQuery(id+"F13.imprint","IMPRINT",EDGE,{"derivedFrom":sQuery(id+"F13.wireOp",EDGE,"E160.1")}),1.0]])]});
            var Q2;
            {var subQ0=sQuery(id+"F13.wireOp",EDGE,"E159.2");var subQ1=sQuery(id+"F13.wireOp",EDGE,"E159.1");var subQ2=makeQuery(id+"F13.imprint","INTERSECT",VERTEX,{"derivedFrom":[subQ1,subQ0]});Q2=makeQuery(id+"F13.imprint","IMPRINT",FACE,{"disambiguationData":[TD([[makeQuery(id+"F13.imprint","IMPRINT",EDGE,{"disambiguationData":[TD([[subQ2,-1.0]])],"derivedFrom":subQ1}),1.0]])]});}
            var Q3;
            {var subQ0=sQuery(id+"F13.wireOp",EDGE,"E159.3");var subQ1=sQuery(id+"F13.wireOp",EDGE,"E159.2");var subQ2=makeQuery(id+"F13.imprint","INTERSECT",VERTEX,{"derivedFrom":[subQ1,subQ0]});Q3=makeQuery(id+"F13.imprint","IMPRINT",FACE,{"disambiguationData":[TD([[makeQuery(id+"F13.imprint","IMPRINT",EDGE,{"disambiguationData":[TD([[subQ2,-1.0]])],"derivedFrom":subQ1}),-1.0]])]});}
            var Q4;
            {var subQ0=sQuery(id+"F13.wireOp",EDGE,"E159.1");var subQ1=sQuery(id+"F13.wireOp",EDGE,"E159.0");var subQ2=makeQuery(id+"F13.imprint","INTERSECT",VERTEX,{"derivedFrom":[subQ1,subQ0]});Q4=makeQuery(id+"F13.imprint","IMPRINT",FACE,{"disambiguationData":[TD([[makeQuery(id+"F13.imprint","IMPRINT",EDGE,{"disambiguationData":[TD([[subQ2,1.0]])],"derivedFrom":subQ1}),1.0]])]});}
            var Q5;
            {var subQ0=sQuery(id+"F13.wireOp",EDGE,"E159.11");var subQ1=sQuery(id+"F13.wireOp",EDGE,"E159.0");var subQ2=makeQuery(id+"F13.imprint","INTERSECT",VERTEX,{"derivedFrom":[subQ1,subQ0]});Q5=makeQuery(id+"F13.imprint","IMPRINT",FACE,{"disambiguationData":[TD([[makeQuery(id+"F13.imprint","IMPRINT",EDGE,{"disambiguationData":[TD([[subQ2,-1.0]])],"derivedFrom":subQ1}),1.0]])]});}
            var Q6;
            {var subQ0=sQuery(id+"F13.wireOp",EDGE,"E159.11");var subQ1=sQuery(id+"F13.wireOp",EDGE,"E159.10");var subQ2=makeQuery(id+"F13.imprint","INTERSECT",VERTEX,{"derivedFrom":[subQ1,subQ0]});Q6=makeQuery(id+"F13.imprint","IMPRINT",FACE,{"disambiguationData":[TD([[makeQuery(id+"F13.imprint","IMPRINT",EDGE,{"disambiguationData":[TD([[subQ2,-1.0]])],"derivedFrom":subQ1}),1.0]])]});}
            var Q7;
            {var subQ0=sQuery(id+"F13.wireOp",EDGE,"E159.10");var subQ1=sQuery(id+"F13.wireOp",EDGE,"E159.9");var subQ2=makeQuery(id+"F13.imprint","INTERSECT",VERTEX,{"derivedFrom":[subQ1,subQ0]});Q7=makeQuery(id+"F13.imprint","IMPRINT",FACE,{"disambiguationData":[TD([[makeQuery(id+"F13.imprint","IMPRINT",EDGE,{"disambiguationData":[TD([[subQ2,1.0]])],"derivedFrom":subQ1}),1.0]])]});}
            var Q8;
            {var subQ0=sQuery(id+"F13.wireOp",EDGE,"E159.9");var subQ1=sQuery(id+"F13.wireOp",EDGE,"E159.8");var subQ2=makeQuery(id+"F13.imprint","INTERSECT",VERTEX,{"derivedFrom":[subQ1,subQ0]});Q8=makeQuery(id+"F13.imprint","IMPRINT",FACE,{"disambiguationData":[TD([[makeQuery(id+"F13.imprint","IMPRINT",EDGE,{"disambiguationData":[TD([[subQ2,1.0]])],"derivedFrom":subQ1}),1.0]])]});}
            var Q9;
            {var subQ1=sQuery(id+"F13.wireOp",EDGE,"E159.7");var subQ3=sQuery(id+"F13.wireOp",EDGE,"E160.0");var subQ4=makeQuery(id+"F13.imprint","INTERSECT",VERTEX,{"derivedFrom":[subQ1,subQ3]});Q9=makeQuery(id+"F13.imprint","IMPRINT",FACE,{"disambiguationData":[TD([[makeQuery(id+"F13.imprint","IMPRINT",EDGE,{"disambiguationData":[TD([[subQ4,1.0]])],"derivedFrom":subQ3}),-1.0]])]});}
            var Q10;
            {var subQ0=sQuery(id+"F13.wireOp",EDGE,"E159.7");var subQ3=sQuery(id+"F13.wireOp",EDGE,"E160.0");var subQ5=makeQuery(id+"F13.imprint","INTERSECT",VERTEX,{"derivedFrom":[subQ0,subQ3]});Q10=makeQuery(id+"F13.imprint","IMPRINT",FACE,{"disambiguationData":[TD([[makeQuery(id+"F13.imprint","IMPRINT",EDGE,{"disambiguationData":[TD([[subQ5,-1.0]])],"derivedFrom":subQ3}),1.0]])]});}
            var Q11;
            {var subQ1=sQuery(id+"F13.wireOp",EDGE,"E159.5");var subQ3=sQuery(id+"F13.wireOp",EDGE,"E160.0");var subQ4=makeQuery(id+"F13.imprint","INTERSECT",VERTEX,{"derivedFrom":[subQ1,subQ3]});Q11=makeQuery(id+"F13.imprint","IMPRINT",FACE,{"disambiguationData":[TD([[makeQuery(id+"F13.imprint","IMPRINT",EDGE,{"disambiguationData":[TD([[subQ4,1.0]])],"derivedFrom":subQ3}),1.0]])]});}
            var Q12;
            {var subQ1=sQuery(id+"F13.wireOp",EDGE,"E159.4");var subQ3=sQuery(id+"F13.wireOp",EDGE,"E160.0");var subQ4=makeQuery(id+"F13.imprint","INTERSECT",VERTEX,{"derivedFrom":[subQ1,subQ3]});Q12=makeQuery(id+"F13.imprint","IMPRINT",FACE,{"disambiguationData":[TD([[makeQuery(id+"F13.imprint","IMPRINT",EDGE,{"disambiguationData":[TD([[subQ4,1.0]])],"derivedFrom":subQ3}),-1.0]])]});}
            var Q13;
            {var subQ4=makeQuery(id+"F10.opExtrude","SWEPT_EDGE",EDGE,{"disambiguationData":[OSD([sQuery(id+"F9.wireOp",EDGE,"E134"),sQuery(id+"F9.wireOp",EDGE,"E137")])]});Q13=makeQuery(id+"F13.imprint","IMPRINT",FACE,{"disambiguationData":[TD([[makeQuery(id+"F13.imprint","IMPRINT",EDGE,{"derivedFrom":subQ4}),-1.0]])]});}
            var Q14;
            {var subQ0=sQuery(id+"F13.wireOp",EDGE,"E159.4");var subQ1=sQuery(id+"F13.wireOp",EDGE,"E159.3");var subQ2=makeQuery(id+"F13.imprint","INTERSECT",VERTEX,{"derivedFrom":[subQ1,subQ0]});Q14=makeQuery(id+"F13.imprint","IMPRINT",FACE,{"disambiguationData":[TD([[makeQuery(id+"F13.imprint","IMPRINT",EDGE,{"disambiguationData":[TD([[subQ2,-1.0]])],"derivedFrom":subQ1}),-1.0]])]});}
            extrude(context, id + "F14", {"entities" : qUnion([Q0, Q1, Q2, Q3, Q4, Q5, Q6, Q7, Q8, Q9, Q10, Q11, Q12, Q13, Q14]), "operationType" : NewBodyOperationType.REMOVE, "oppositeDirection" : true, "depth" : 5 * mm, "hasSecondDirection" : true, "secondDirectionOppositeDirection" : false, "secondDirectionDepth" : 5 * mm});
        }
        {
            var Q0;
            Q0=makeQuery(id+"F11.imprint","IMPRINT",FACE,{"disambiguationData":[TD([[makeQuery(id+"F11.imprint","IMPRINT",EDGE,{"derivedFrom":sQuery(id+"F11.wireOp",EDGE,"E158")}),-1.0]])]});
            var Q1;
            {var subQ0=sQuery(id+"F11.wireOp",EDGE,"E142.3");var subQ1=sQuery(id+"F11.wireOp",EDGE,"E141");var subQ2=makeQuery(id+"F11.imprint","INTERSECT",VERTEX,{"derivedFrom":[subQ1,subQ0]});Q1=makeQuery(id+"F11.imprint","IMPRINT",FACE,{"disambiguationData":[TD([[makeQuery(id+"F11.imprint","IMPRINT",EDGE,{"disambiguationData":[TD([[subQ2,-1.0]])],"derivedFrom":subQ1}),1.0]])]});}
            var Q2;
            {var subQ0=sQuery(id+"F11.wireOp",EDGE,"E145.1");var subQ1=sQuery(id+"F11.wireOp",EDGE,"E141");var subQ2=makeQuery(id+"F11.imprint","INTERSECT",VERTEX,{"derivedFrom":[subQ1,subQ0]});Q2=makeQuery(id+"F11.imprint","IMPRINT",FACE,{"disambiguationData":[TD([[makeQuery(id+"F11.imprint","IMPRINT",EDGE,{"disambiguationData":[TD([[subQ2,-1.0]])],"derivedFrom":subQ1}),1.0]])]});}
            var Q3;
            {var subQ0=sQuery(id+"F11.wireOp",EDGE,"E142.1");var subQ1=sQuery(id+"F11.wireOp",EDGE,"E141");var subQ2=makeQuery(id+"F11.imprint","INTERSECT",VERTEX,{"derivedFrom":[subQ1,subQ0]});Q3=makeQuery(id+"F11.imprint","IMPRINT",FACE,{"disambiguationData":[TD([[makeQuery(id+"F11.imprint","IMPRINT",EDGE,{"disambiguationData":[TD([[subQ2,-1.0]])],"derivedFrom":subQ1}),1.0]])]});}
            var Q4;
            {var subQ1=makeQuery(id+"F10.opExtrude","SWEPT_EDGE",EDGE,{"disambiguationData":[OSD([sQuery(id+"F9.wireOp",EDGE,"E116"),sQuery(id+"F9.wireOp",EDGE,"E117"),sQuery(id+"F9.wireOp",EDGE,"E120")])]});Q4=makeQuery(id+"F11.imprint","IMPRINT",FACE,{"disambiguationData":[TD([[makeQuery(id+"F11.imprint","IMPRINT",EDGE,{"derivedFrom":subQ1}),1.0]])]});}
            var Q5;
            {var subQ0=sQuery(id+"F11.wireOp",EDGE,"E156");var subQ1=sQuery(id+"F11.wireOp",EDGE,"E141");var subQ2=makeQuery(id+"F11.imprint","INTERSECT",VERTEX,{"derivedFrom":[subQ1,subQ0]});Q5=makeQuery(id+"F11.imprint","IMPRINT",FACE,{"disambiguationData":[TD([[makeQuery(id+"F11.imprint","IMPRINT",EDGE,{"disambiguationData":[TD([[subQ2,-1.0]])],"derivedFrom":subQ1}),1.0]])]});}
            var Q6;
            {var subQ23=sQuery(id+"F11.wireOp",EDGE,"E146");var subQ24=sQuery(id+"F11.wireOp",EDGE,"E147");Q6=makeQuery(id+"F12.boolean.opBoolean","COPY",FACE,{"disambiguationData":[TD([makeQuery(id+"F12.opExtrude","SWEPT_FACE",FACE,{"disambiguationData":[OSD([subQ23])]})])],"derivedFrom":makeQuery(id+"F12.opExtrude","CAP_FACE",FACE,{"disambiguationData":[OSD([sQuery(id+"F11.wireOp",EDGE,"E141"),sQuery(id+"F11.wireOp",EDGE,"E142.0"),sQuery(id+"F11.wireOp",EDGE,"E142.1"),sQuery(id+"F11.wireOp",EDGE,"E142.2"),sQuery(id+"F11.wireOp",EDGE,"E142.3"),sQuery(id+"F11.wireOp",EDGE,"E143"),sQuery(id+"F11.wireOp",EDGE,"E144"),sQuery(id+"F11.wireOp",EDGE,"E145.0"),sQuery(id+"F11.wireOp",EDGE,"E145.1"),subQ23,subQ24,sQuery(id+"F11.wireOp",EDGE,"E156"),sQuery(id+"F11.wireOp",EDGE,"E157")])],"isStart":true})});}
            extrude(context, id + "F15", {"entities" : qUnion([Q0, Q1, Q2, Q3, Q4, Q5]), "endBound" : BoundingType.UP_TO_SURFACE, "oppositeDirection" : true, "endBoundEntityFace" : qUnion([Q6]), "depth" : 5 * mm});
        }
        {
            var Q0;
            Q0=makeQuery(id+"F13.imprint","IMPRINT",FACE,{"disambiguationData":[TD([[makeQuery(id+"F13.imprint","IMPRINT",EDGE,{"derivedFrom":sQuery(id+"F13.wireOp",EDGE,"E160.1")}),1.0]])]});
            var Q1;
            {var subQ0=sQuery(id+"F13.wireOp",EDGE,"E159.2");var subQ1=sQuery(id+"F13.wireOp",EDGE,"E159.1");var subQ2=makeQuery(id+"F13.imprint","INTERSECT",VERTEX,{"derivedFrom":[subQ1,subQ0]});Q1=makeQuery(id+"F13.imprint","IMPRINT",FACE,{"disambiguationData":[TD([[makeQuery(id+"F13.imprint","IMPRINT",EDGE,{"disambiguationData":[TD([[subQ2,-1.0]])],"derivedFrom":subQ1}),1.0]])]});}
            var Q2;
            {var subQ0=sQuery(id+"F13.wireOp",EDGE,"E159.11");var subQ1=sQuery(id+"F13.wireOp",EDGE,"E159.10");var subQ2=makeQuery(id+"F13.imprint","INTERSECT",VERTEX,{"derivedFrom":[subQ1,subQ0]});Q2=makeQuery(id+"F13.imprint","IMPRINT",FACE,{"disambiguationData":[TD([[makeQuery(id+"F13.imprint","IMPRINT",EDGE,{"disambiguationData":[TD([[subQ2,-1.0]])],"derivedFrom":subQ1}),1.0]])]});}
            var Q3;
            {var subQ1=sQuery(id+"F13.wireOp",EDGE,"E159.7");var subQ3=sQuery(id+"F13.wireOp",EDGE,"E160.0");var subQ4=makeQuery(id+"F13.imprint","INTERSECT",VERTEX,{"derivedFrom":[subQ1,subQ3]});Q3=makeQuery(id+"F13.imprint","IMPRINT",FACE,{"disambiguationData":[TD([[makeQuery(id+"F13.imprint","IMPRINT",EDGE,{"disambiguationData":[TD([[subQ4,1.0]])],"derivedFrom":subQ3}),-1.0]])]});}
            var Q4;
            {var subQ4=makeQuery(id+"F10.opExtrude","SWEPT_EDGE",EDGE,{"disambiguationData":[OSD([sQuery(id+"F9.wireOp",EDGE,"E134"),sQuery(id+"F9.wireOp",EDGE,"E137")])]});Q4=makeQuery(id+"F13.imprint","IMPRINT",FACE,{"disambiguationData":[TD([[makeQuery(id+"F13.imprint","IMPRINT",EDGE,{"derivedFrom":subQ4}),-1.0]])]});}
            var Q5;
            {var subQ1=sQuery(id+"F13.wireOp",EDGE,"E159.4");var subQ3=sQuery(id+"F13.wireOp",EDGE,"E160.0");var subQ4=makeQuery(id+"F13.imprint","INTERSECT",VERTEX,{"derivedFrom":[subQ1,subQ3]});Q5=makeQuery(id+"F13.imprint","IMPRINT",FACE,{"disambiguationData":[TD([[makeQuery(id+"F13.imprint","IMPRINT",EDGE,{"disambiguationData":[TD([[subQ4,1.0]])],"derivedFrom":subQ3}),-1.0]])]});}
            var Q6;
            {var subQ23=sQuery(id+"F13.wireOp",EDGE,"E159.3");var subQ24=sQuery(id+"F13.wireOp",EDGE,"E159.9");Q6=makeQuery(id+"F14.boolean.opBoolean","COPY",FACE,{"disambiguationData":[TD([makeQuery(id+"F14.opExtrude","SWEPT_FACE",FACE,{"disambiguationData":[OSD([subQ23])]})])],"derivedFrom":makeQuery(id+"F14.opExtrude","CAP_FACE",FACE,{"disambiguationData":[OSD([sQuery(id+"F13.wireOp",EDGE,"E159.0"),sQuery(id+"F13.wireOp",EDGE,"E159.1"),sQuery(id+"F13.wireOp",EDGE,"E159.2"),subQ23,sQuery(id+"F13.wireOp",EDGE,"E159.4"),sQuery(id+"F13.wireOp",EDGE,"E159.5"),sQuery(id+"F13.wireOp",EDGE,"E159.6"),sQuery(id+"F13.wireOp",EDGE,"E159.7"),sQuery(id+"F13.wireOp",EDGE,"E159.8"),subQ24,sQuery(id+"F13.wireOp",EDGE,"E159.10"),sQuery(id+"F13.wireOp",EDGE,"E159.11"),sQuery(id+"F13.wireOp",EDGE,"E160.0")])],"isStart":false})});}
            extrude(context, id + "F16", {"entities" : qUnion([Q0, Q1, Q2, Q3, Q4, Q5]), "endBound" : BoundingType.UP_TO_SURFACE, "oppositeDirection" : true, "endBoundEntityFace" : qUnion([Q6]), "depth" : 2 * mm});
        }
        {
            var Q0;
            Q0=makeQuery(id+"F16.opExtrude","CAP_FACE",FACE,{"disambiguationData":[OSD([sQuery(id+"F13.wireOp",EDGE,"E160.0"),sQuery(id+"F13.wireOp",EDGE,"E160.1")])],"isStart":false});
            var sketch = newSketch(context, id + "F17", { "sketchPlane" : qUnion([Q0])});
            skLineSegment(sketch, "E161.bottom", {"start": v(-25.19, 2) * mm, "end": v(-22.19, 2) * mm});
            skLineSegment(sketch, "E161.top", {"start": v(-25.19, -2) * mm, "end": v(-22.19, -2) * mm});
            skLineSegment(sketch, "E161.left", {"start": v(-25.19, 2) * mm, "end": v(-25.19, -2) * mm});
            skLineSegment(sketch, "E161.right", {"start": v(-22.19, 2) * mm, "end": v(-22.19, -2) * mm});
            skPoint(sketch, "E161.middle", {"position": v(-23.69, 0) * mm});
            skSolve(sketch);
        }
        {
            var Q0;
            Q0=qCreatedBy(makeId("Front.planeOp"),FACE);
            var sketch = newSketch(context, id + "F18", { "sketchPlane" : qUnion([Q0])});
            skLineSegment(sketch, "E162.0", {"start": v(-67.32, -74.22) * mm, "end": v(-68.18, -73.72) * mm, "construction": true});
            skLineSegment(sketch, "E162.1", {"start": v(-69.15, -67.4) * mm, "end": v(-64.82, -69.9) * mm, "construction": true});
            skLineSegment(sketch, "E162.2", {"start": v(37.68, 107.64) * mm, "end": v(36.82, 108.14) * mm, "construction": true});
            skLineSegment(sketch, "E162.3", {"start": v(30.85, 105.81) * mm, "end": v(35.18, 103.31) * mm, "construction": true});
            skPoint(sketch, "E163.0", {"position": v(34.22, 109.64) * mm});
            skPoint(sketch, "E164.0", {"position": v(36.82, 108.14) * mm});
            skLineSegment(sketch, "E165", {"start": v(34.22, 109.64) * mm, "end": v(31.72, 105.31) * mm});
            skLineSegment(sketch, "E166", {"start": v(36.82, 108.14) * mm, "end": v(34.32, 103.81) * mm});
            skLineSegment(sketch, "E167", {"start": v(34.32, 103.81) * mm, "end": v(29.31, 95.14) * mm});
            skLineSegment(sketch, "E168", {"start": v(-65.68, -69.4) * mm, "end": v(-68.18, -73.72) * mm});
            skLineSegment(sketch, "E169", {"start": v(31.72, 105.31) * mm, "end": v(26.71, 96.64) * mm});
            skLineSegment(sketch, "E170", {"start": v(-68.28, -67.9) * mm, "end": v(-70.78, -72.22) * mm});
            skLineSegment(sketch, "E171", {"start": v(-70.78, -72.22) * mm, "end": v(-71.65, -71.72) * mm, "construction": true});
            skLineSegment(sketch, "E172", {"start": v(-68.18, -73.72) * mm, "end": v(-70.78, -72.22) * mm});
            skLineSegment(sketch, "E173", {"start": v(34.22, 109.64) * mm, "end": v(33.35, 110.14) * mm, "construction": true});
            skLineSegment(sketch, "E174", {"start": v(36.82, 108.14) * mm, "end": v(34.22, 109.64) * mm});
            skLineSegment(sketch, "E175", {"start": v(-65.68, -69.4) * mm, "end": v(31.72, 105.31) * mm, "construction": true});
            skLineSegment(sketch, "E176", {"start": v(-63.28, -59.22) * mm, "end": v(-68.28, -67.9) * mm});
            skLineSegment(sketch, "E177", {"start": v(-60.68, -60.72) * mm, "end": v(-65.68, -69.4) * mm});
            skLineSegment(sketch, "E178", {"start": v(26.71, 96.64) * mm, "end": v(-63.28, -59.22) * mm, "construction": true});
            skLineSegment(sketch, "E179", {"start": v(29.31, 95.14) * mm, "end": v(-60.68, -60.72) * mm, "construction": true});
            skArc(sketch, "E180", {"start": v(26.71, 96.64) * mm, "mid": v(-94.92, 62.96) * mm, "end": v(-63.28, -59.22) * mm});
            skArc(sketch, "E181", {"start": v(29.31, 95.14) * mm, "mid": v(28.02, 95.9) * mm, "end": v(26.71, 96.64) * mm, "construction": true});
            skArc(sketch, "E182", {"start": v(-63.28, -59.22) * mm, "mid": v(-61.98, -59.98) * mm, "end": v(-60.68, -60.72) * mm, "construction": true});
            skArc(sketch, "E183", {"start": v(-60.68, -60.72) * mm, "mid": v(60.96, -27.04) * mm, "end": v(29.31, 95.14) * mm});
            skSolve(sketch);
        }
        {
            var Q0;
            Q0=makeQuery(id+"F18.imprint","IMPRINT",FACE,{"disambiguationData":[TD([[makeQuery(id+"F18.imprint","IMPRINT",EDGE,{"derivedFrom":sQuery(id+"F18.wireOp",EDGE,"E165")}),1.0]])]});
            extrude(context, id + "F19", {"entities" : qUnion([Q0]), "depth" : 2 * mm, "hasSecondDirection" : true, "secondDirectionOppositeDirection" : true, "secondDirectionDepth" : 2 * mm});
        }
    });
